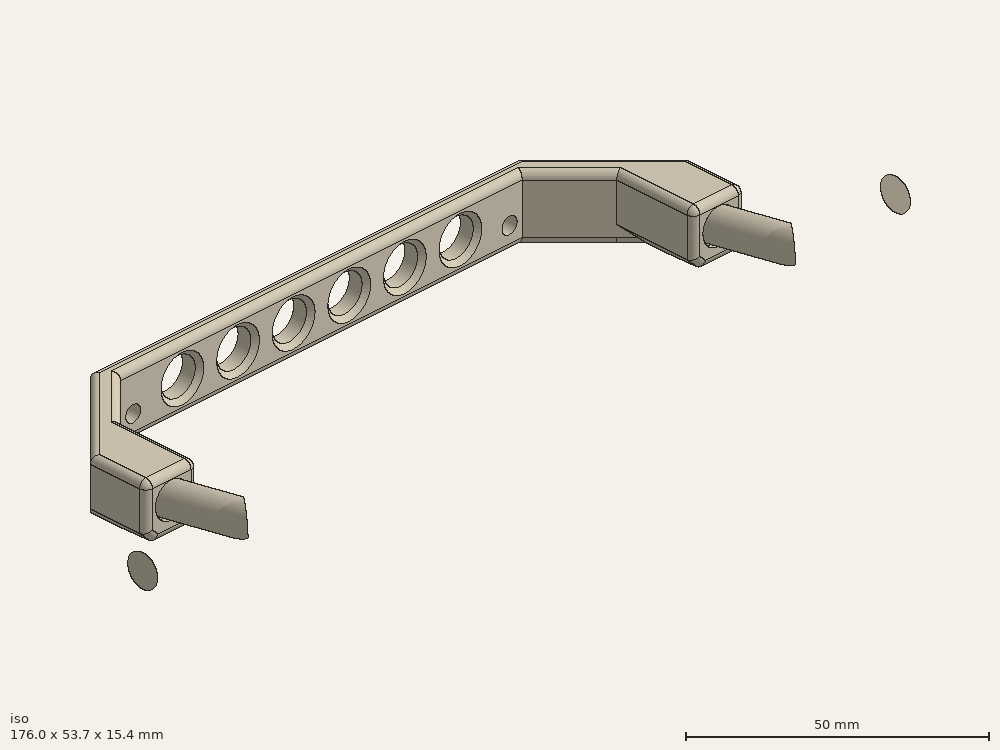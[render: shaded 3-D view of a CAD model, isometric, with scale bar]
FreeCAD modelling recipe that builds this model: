
FCSTD DOCUMENT  (FreeCAD 0.15R4671 (Git))
Label: rock-sliders
License: All rights reserved
LicenseURL: http://en.wikipedia.org/wiki/All_rights_reserved
objects: Part::Cylinder×8, Part::MultiFuse×4, Part::Cut×4, Sketcher::SketchObject×3, PartDesign::Pad×3, Part::Chamfer×2, Part::Mirroring×1, Part::Fillet×1
note: 29 computed .brp shape members not serialized (recipe doc carries the construction recipe); baked Part::Feature solids carry a one-line shape summary decoded from their .brp

FEATURE [Sketcher::SketchObject] Sketch
  sketch-geometry (14):
    g0: LineSegment StartX=-70 StartY=-23 StartZ=0 EndX=-70 EndY=-10 EndZ=0
    g1: LineSegment StartX=-70 StartY=-10 StartZ=0 EndX=-50 EndY=10 EndZ=0
    g2: LineSegment StartX=-50 StartY=10 StartZ=0 EndX=50 EndY=10 EndZ=0
    g3: LineSegment StartX=50 StartY=10 StartZ=0 EndX=70 EndY=-10 EndZ=0
    g4: LineSegment StartX=70 StartY=-10 StartZ=0 EndX=70 EndY=-23 EndZ=0
    g5: LineSegment StartX=70 StartY=-23 StartZ=0 EndX=58 EndY=-23 EndZ=0
    g6: LineSegment StartX=58 StartY=-23 StartZ=0 EndX=58 EndY=-5.07107 EndZ=0
    g7: LineSegment StartX=58 StartY=-5.07107 StartZ=0 EndX=46.9289 EndY=6 EndZ=0
    g8: LineSegment StartX=46.9289 StartY=6 StartZ=0 EndX=-46.9289 EndY=6 EndZ=0
    g9: LineSegment StartX=-46.9289 StartY=6 StartZ=0 EndX=-58 EndY=-5.07107 EndZ=0
    g10: LineSegment StartX=-58 StartY=-5.07107 StartZ=0 EndX=-58 EndY=-23 EndZ=0
    g11: LineSegment StartX=-58 StartY=-23 StartZ=0 EndX=-70 EndY=-23 EndZ=0
    g12: LineSegment [constr] StartX=-58 StartY=-23 StartZ=0 EndX=58 EndY=-23 EndZ=0
    g13: LineSegment [constr] StartX=-58 StartY=-5.07107 StartZ=0 EndX=-61.5355 EndY=-1.53553 EndZ=0
  constraints (41):
    c: Vertical(g0)
    c: Coincident(g0,g1)
    c: Coincident(g1,g2)
    c: Horizontal(g2)
    c: Coincident(g2,g3)
    c: Coincident(g3,g4)
    c: Vertical(g4)
    c: Horizontal(g5)
    c: Coincident(g5,g6)
    c: Vertical(g6)
    c: Coincident(g6,g7)
    c: Coincident(g7,g8)
    c: Horizontal(g8)
    c: Coincident(g8,g9)
    c: Coincident(g9,g10)
    c: Coincident(g10,g11)
    c: Coincident(g0,g11)
    c: Horizontal(g11)
    c: Vertical(g10)
    c: Distance(g2) = 100
    c: DistanceX(g0,g4) = 140
    c: Coincident(g4,g5)
    c: Equal(g11,g5)
    c: Equal(g1,g3)
    c: Equal(g9,g7)
    c: Symmetric(g1,g2,g-2)
    c: Equal(g10,g6)
    c: Coincident(g12,g10)
    c: Coincident(g12,g5)
    c: Horizontal(g12)
    c: DistanceY(g2,g7) = -4
    c: Angle(g1,g2) = 2.35619
    c: Angle(g2,g3) = 2.35619
    c: DistanceY(g1,g0) = -33
    c: Distance(g11) = 12
    c: Parallel(g1,g9)
    c: Coincident(g13,g9)
    c: PointOnObject(g13,g1)
    c: Perpendicular(g13,g1)
    c: Distance(g13) = 5
    c: DistanceY(g-1,g2) = 10
FEATURE [PartDesign::Pad] Pad
  Length = 14
  Length2 = 100
  Sketch = -> Sketch
  Type = 0
FEATURE [Part::Cylinder] Cylinder
  Angle = 360
  Height = 40
  Placement = pos=(0,0,21) rot=(0,0,1;0rad)
  Radius = 3.8
FEATURE [Part::Cylinder] Cylinder001
  Angle = 360
  Height = 50
  Placement = pos=(0,0,-19) rot=(0,0,1;0rad)
  Radius = 2.25
FEATURE [Part::Cylinder] Cylinder002
  Angle = 360
  Height = 40
  Placement = pos=(0,0,-24) rot=(0,0,1;0rad)
  Radius = 3.8
FEATURE [Part::MultiFuse] Fusion
  Placement = pos=(64,0,4.5) rot=(1,0,0;1.39626rad)
  Shapes = -> [Cylinder001,Cylinder,Cylinder002]
FEATURE [Part::Mirroring] Part__Mirroring  label="Fusion (Mirror #1)"
  Base = (0,0,0)
  Normal = (1,0,0)
  Source = -> Fusion
FEATURE [Part::MultiFuse] Fusion001
  Shapes = -> [Fusion,Part__Mirroring]
FEATURE [Part::Cut] Cut
  Base = -> Pad
  Tool = -> Fusion001
FEATURE [Part::Chamfer] Chamfer
  Base = -> Cut
  Edges = 4 edges r=4: [Edge3,Edge15,Edge17,Edge21]
FEATURE [Part::Cylinder] Cylinder003
  Angle = 360
  Height = 176
  Placement = pos=(-88,-51,0) rot=(0,1,0;1.5708rad)
  Radius = 3.5
FEATURE [Part::Cylinder] Cylinder004
  Angle = 360
  Height = 20
  Placement = pos=(-64,-51,0) rot=(-1,0,0;1.5708rad)
  Radius = 3.5
FEATURE [Part::Cylinder] Cylinder005
  Angle = 360
  Height = 20
  Placement = pos=(64,-51,0) rot=(-1,0,0;1.5708rad)
  Radius = 3.5
FEATURE [Part::MultiFuse] Fusion002
  Placement = pos=(0,10,3) rot=(-1,0,0;0.174533rad)
  Shapes = -> [Cylinder004,Cylinder003,Cylinder005]
FEATURE [Part::Cylinder] Cylinder006
  Angle = 360
  Height = 30
  Placement = pos=(44,20,4) rot=(1,0,0;1.5708rad)
  Radius = 1.75
FEATURE [Part::Cylinder] Cylinder007
  Angle = 360
  Height = 30
  Placement = pos=(-44,20,4) rot=(1,0,0;1.5708rad)
  Radius = 1.75
FEATURE [Part::MultiFuse] Fusion003
  Placement = pos=(0,0,1) rot=(0,0,1;0rad)
  Shapes = -> [Cylinder007,Cylinder006]
FEATURE [Part::Cut] Cut001
  Base = -> Chamfer
  Tool = -> Fusion003
FEATURE [Sketcher::SketchObject] Sketch001
  Placement = pos=(90,0,0) rot=(0.57735,0.57735,0.57735;2.0944rad)
  sketch-geometry (3):
    g0: LineSegment StartX=-29.3466 StartY=3.17112 StartZ=0 EndX=2.81582 EndY=-2.49999 EndZ=0
    g1: LineSegment StartX=2.81582 StartY=-2.49999 StartZ=0 EndX=-29.3466 EndY=-2.49999 EndZ=0
    g2: LineSegment StartX=-29.3466 StartY=-2.49999 StartZ=0 EndX=-29.3466 EndY=3.17112 EndZ=0
  constraints (6):
    c: Coincident(g0,g1)
    c: Horizontal(g1)
    c: Coincident(g1,g2)
    c: Coincident(g2,g0)
    c: Vertical(g2)
    c: Angle(g0,g1) = 0.174533
FEATURE [PartDesign::Pad] Pad001
  Length = 185
  Length2 = 100
  Placement = pos=(90,0,0) rot=(0.57735,0.57735,0.57735;2.0944rad)
  Reversed = true
  Sketch = -> Sketch001
  Type = 0
FEATURE [Part::Cut] Cut002
  Base = -> Cut001
  Tool = -> Pad001
FEATURE [Sketcher::SketchObject] Sketch002
  Placement = pos=(0,0,0) rot=(0,0.707107,0.707107;3.14159rad)
  sketch-geometry (11):
    g0: Circle CenterX=-32.5 CenterY=7 CenterZ=0 NormalX=0 NormalY=0 NormalZ=1 Radius=4
    g1: Circle CenterX=-19.5 CenterY=7 CenterZ=0 NormalX=0 NormalY=0 NormalZ=1 Radius=4
    g2: Circle CenterX=-6.5 CenterY=7 CenterZ=0 NormalX=0 NormalY=0 NormalZ=1 Radius=4
    g3: Circle CenterX=6.5 CenterY=7 CenterZ=0 NormalX=0 NormalY=0 NormalZ=1 Radius=4
    g4: Circle CenterX=19.5 CenterY=7 CenterZ=0 NormalX=0 NormalY=0 NormalZ=1 Radius=4
    g5: Circle CenterX=32.5 CenterY=7 CenterZ=0 NormalX=0 NormalY=0 NormalZ=1 Radius=4
    g6: LineSegment [constr] StartX=-32.5 StartY=7 StartZ=0 EndX=-19.5 EndY=7 EndZ=0
    g7: LineSegment [constr] StartX=-19.5 StartY=7 StartZ=0 EndX=-6.5 EndY=7 EndZ=0
    g8: LineSegment [constr] StartX=-6.5 StartY=7 StartZ=0 EndX=6.5 EndY=7 EndZ=0
    g9: LineSegment [constr] StartX=6.5 StartY=7 StartZ=0 EndX=19.5 EndY=7 EndZ=0
    g10: LineSegment [constr] StartX=19.5 StartY=7 StartZ=0 EndX=32.5 EndY=7 EndZ=0
  constraints (28):
    c: Equal(g0,g1)
    c: Equal(g1,g2)
    c: Equal(g2,g3)
    c: Equal(g3,g4)
    c: Equal(g4,g5)
    c: Coincident(g6,g0)
    c: Coincident(g6,g1)
    c: Coincident(g6,g7)
    c: Coincident(g7,g2)
    c: Coincident(g7,g8)
    c: Coincident(g8,g3)
    c: Horizontal(g8)
    c: Coincident(g8,g9)
    c: Coincident(g9,g4)
    c: Coincident(g9,g10)
    c: Coincident(g10,g5)
    c: Horizontal(g10)
    c: Horizontal(g6)
    c: Horizontal(g7)
    c: Horizontal(g9)
    c: Equal(g6,g7)
    c: Equal(g7,g8)
    c: Equal(g8,g9)
    c: Equal(g9,g10)
    c: Symmetric(g0,g5,g-2)
    c: Distance(g6) = 13
    c: Distance(g-1,g8) = 7
    c: Radius(g2) = 4
FEATURE [PartDesign::Pad] Pad002
  Length = 20
  Length2 = 100
  Placement = pos=(0,0,0) rot=(0,0.707107,0.707107;3.14159rad)
  Sketch = -> Sketch002
  Type = 0
FEATURE [Part::Cut] Cut003
  Base = -> Cut002
  Tool = -> Pad002
FEATURE [Part::Chamfer] Chamfer001
  Base = -> Cut003
  Edges = 6 edges r=1: [Edge69,Edge70,Edge71,Edge72,Edge73,Edge74]
FEATURE [Part::Fillet] Fillet
  Base = -> Chamfer001
  Edges = 25 edges r=1.5: [Edge3,Edge4,Edge17,Edge19,Edge24,Edge31,Edge32,Edge33,Edge34,Edge35,Edge36,Edge37,Edge38,Edge39,Edge40,Edge59,Edge61,Edge63,Edge67,Edge70,Edge71,Edge75,Edge87,Edge88,Edge90]
